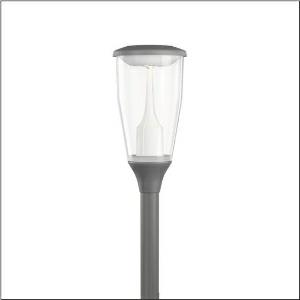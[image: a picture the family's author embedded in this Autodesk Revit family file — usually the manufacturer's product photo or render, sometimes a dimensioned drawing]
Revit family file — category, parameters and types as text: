
# Revit family: dl_11_iq___p1_0a_5xa5565ff14hp00022_87ad
name_source: partatom
category: Lighting Fixtures
units: mm (PartAtom-declared; Revit-internal decimal feet)

## family parameters
Cut with Voids When Loaded = No
Host = Face
Light Source = No
Part Type = Normal
Room Calculation Point = No
Round Connector Dimension = Use Diameter
Shared = No

## types (1)
- --- (1 x LED, 4780 lm, 33.6 W, 3000K)
    Apparent Load = 34 VA
    CIE Flux Codes = 33 63 91 94 100
    Color Rendering = 70
    Color Temperature = 3000K
    Default Elevation = 1800 mm
    Description = DL 11 iQ, mast luminaire, Module 540 iQ-SR, primary light control with 3 zone facetted reflector, of plastic, silver coated, highly specular, structured, primary optical cover: cover, of PMMA, transparent, light distribution: P1.0a, light emission: direct distribution, primary light characteristic: asymmetric, installation type: post-top, LED, High Power LED, light colour: 730, colour temperature: 3000K, control gear: iQ Street-Remote, control: Street-Remote, Auto-Match, Temp-Guard, Lumen-Switch, Night-Set, Smart-Wire, Light-Fading, Desk-Remote (wireless, voltage-free reading and setting of iQ features in the workshop via application-optimized NFC function/RFID function), optimised constant luminous flux control (CLO 2.0), mains connection: 220..240V, AC, 50/60Hz, connection cable pre-assembled, cable length: 5,5m, start of lifetime: 34W, end of service life: 36W, luminaire housing, upper part, of diecast aluminium, coated, SITECO metallic grey (DB 702S), spigot size: 60mm (post-top), mounting height: 3..5m, post-top mast mounting element, of diecast aluminium, coated, SITECO metallic grey (DB 702S), Module 540 iQ-SR, traffic white (RAL 9016), equipment: Power, protection rating (complete): IP66, insulation class (complete): insulation class II (safety insulation), certification: CE, ENEC, ENEC+, VDE, impact resistance: IK07, packaging unit: 1 piece

Light Distribution: P1.0a
    Height = 665 mm
    Lamp = 1 x LED
    Lamp Light Flux = 4780 lm
    Lamp Power = 33.6 W
    Lamp count = 1
    Length = 334 mm
    Luminous efficacy = 142 lm/W
    Manufacturer = Siteco
    ModVariant = No
    Model = 5XA5565FF14HP00022
    Number of Poles = 1
    OnlyDefault = Yes
    Power Factor = 1
    Product Name = DL 11 iQ | P1.0a
    Product group = mast luminaire | pylon top
    ProductGroupID = 6100
    Protection Class = Protection class II
    Protection Degree = IP 66
    RLX_Detail_Level = 1
    RLX_Emergency_Light_Flux = 0 lm
    RLX_Emergency_Type = 0
    RLX_Emergency_Type_DB = No
    RlxData = <blob elided: 104353 chars, md5=054fb9fa>
    Socket = socket
    Standby Power = 0 W
    System Light Flux = 4780 lm
    System Power = 34 W
    Type Comments = factory setting: luminous flux: 100 % | dim-lin: 254 | 695 mA
    Type Image = l_1258354.jpg
    URL = http://relux.com
    VarID = @adj_040007
    Voltage = 0 V
    Weight = 0.00 kg
    Width = 0 mm  [stored 0 ft]

note: [stored X ft] marks values corroborated as IEEE doubles in the binary element streams (Revit-internal decimal feet)

## geometry (parser evidence)
native form markers: Blend x4, Sweep x10
no freeform markers — native parametric forms only
